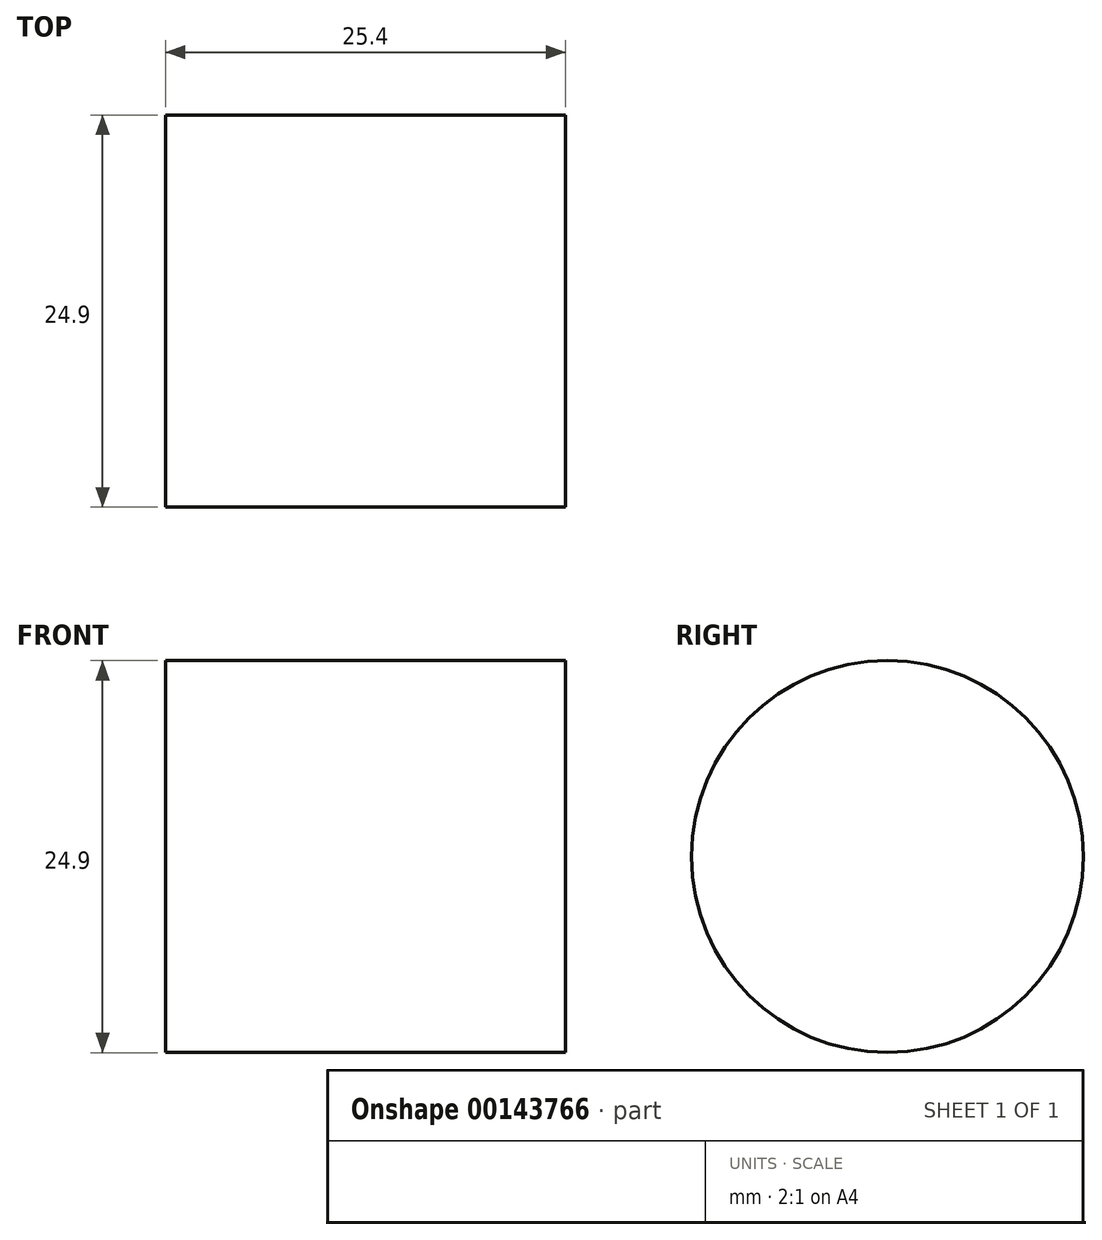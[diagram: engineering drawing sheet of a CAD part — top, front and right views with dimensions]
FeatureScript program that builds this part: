
annotation { "Feature Type Name" : "Feature", "Feature Type Description" : "" }
export const myFeature = defineFeature(function(context is Context, id is Id, definition is map)
    precondition{}
    {
        {
            var Q0;
            Q0=qCreatedBy(makeId("Right.planeOp"),FACE);
            var sketch = newSketch(context, id + "F0", { "sketchPlane" : qUnion([Q0])});
            skCircle(sketch, "E0", {"center": v(0, 0) * mm, "radius": 12.45 * mm});
            skSolve(sketch);
        }
        {
            var Q0;
            Q0 = qSketchRegion(id + "F0", true);
            extrude(context, id + "F1", {"entities" : qUnion([Q0]), "depth" : 25.4 * mm});
        }
    });
